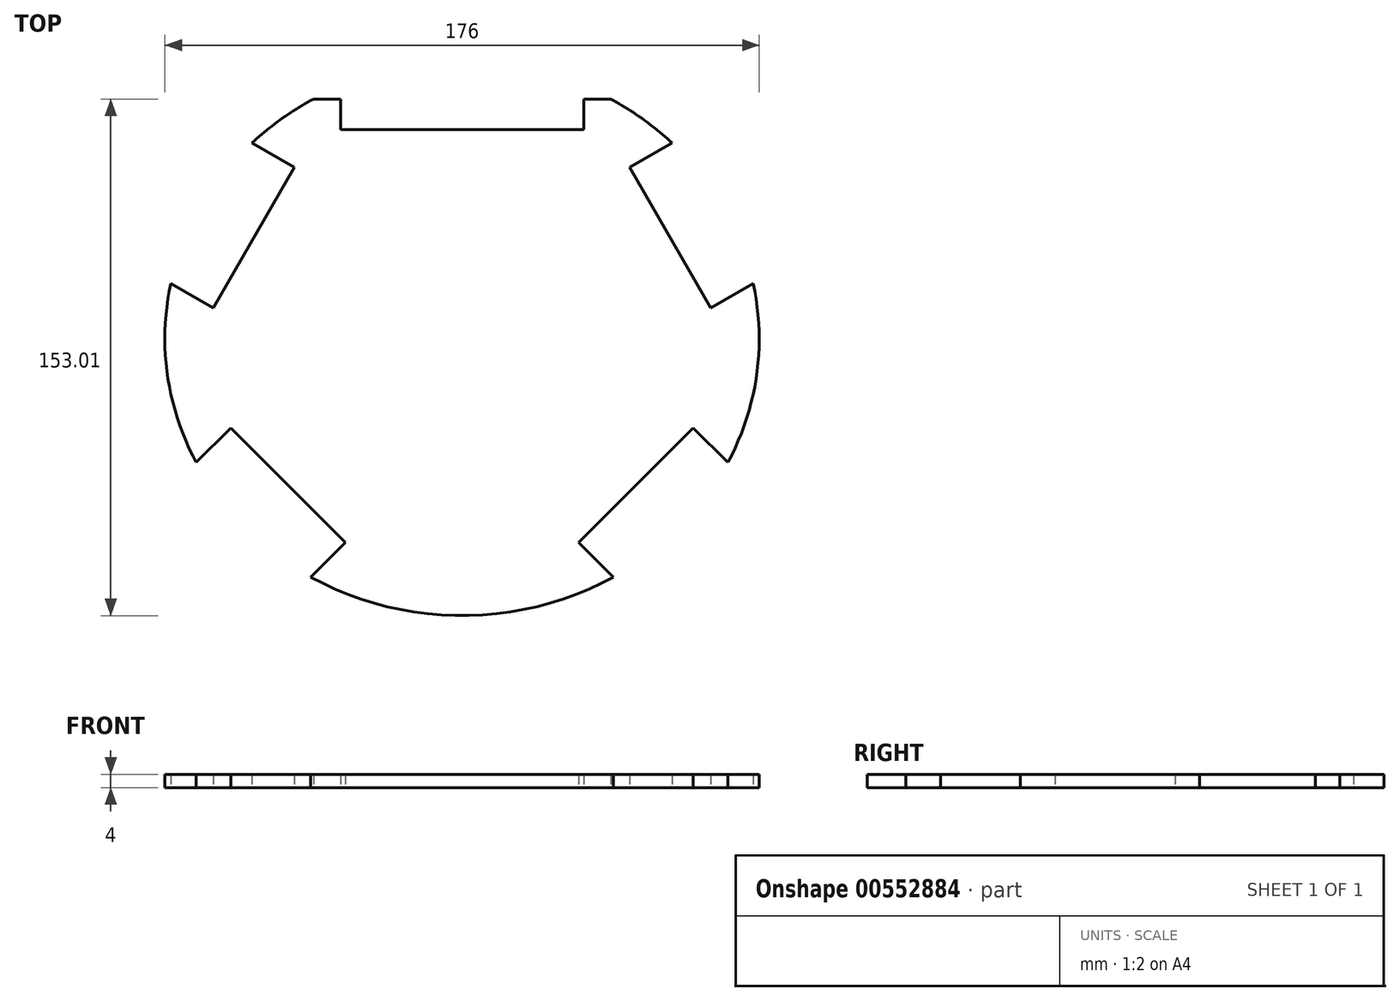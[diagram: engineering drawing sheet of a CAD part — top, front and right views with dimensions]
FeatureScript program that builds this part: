
annotation { "Feature Type Name" : "Feature", "Feature Type Description" : "" }
export const myFeature = defineFeature(function(context is Context, id is Id, definition is map)
    precondition{}
    {
        {
            var Q0;
            Q0=qCreatedBy(makeId("Top.planeOp"),FACE);
            var sketch = newSketch(context, id + "F0", { "sketchPlane" : qUnion([Q0])});
            skEllipticalArc(sketch, "E0", {});
            skLineSegment(sketch, "E1", {"start": v(-44, 71.01) * mm, "end": v(-36, 71.01) * mm});
            skLineSegment(sketch, "E2", {"start": v(-75.53, 0) * mm, "end": v(76.85, 0) * mm, "construction": true});
            skPoint(sketch, "E3.middle", {"position": v(0, 71.01) * mm});
            skLineSegment(sketch, "E4.bottom", {"start": v(36, 62.01) * mm, "end": v(-36, 62.01) * mm});
            skLineSegment(sketch, "E4.left", {"start": v(36, 62.01) * mm, "end": v(36, 71.01) * mm});
            skLineSegment(sketch, "E4.right", {"start": v(-36, 62.01) * mm, "end": v(-36, 71.01) * mm});
            skEllipticalArc(sketch, "E5.trimOffspring", {});
            skEllipticalArc(sketch, "E6.trimOffspring", {});
            skEllipticalArc(sketch, "E7.trimOffspring", {});
            skEllipticalArc(sketch, "E8.trimOffspring", {});
            skLineSegment(sketch, "E9", {"start": v(-86.22, 16.42) * mm, "end": v(-73.66, 9.17) * mm});
            skLineSegment(sketch, "E10", {"start": v(-73.66, 9.17) * mm, "end": v(-49.66, 50.74) * mm});
            skLineSegment(sketch, "E11", {"start": v(-49.66, 50.74) * mm, "end": v(-62.22, 58) * mm});
            skLineSegment(sketch, "E12", {"start": v(-78.72, -36.65) * mm, "end": v(-68.47, -26.4) * mm});
            skLineSegment(sketch, "E13", {"start": v(-68.47, -26.4) * mm, "end": v(-34.53, -60.34) * mm});
            skLineSegment(sketch, "E14", {"start": v(-34.53, -60.34) * mm, "end": v(-44.78, -70.59) * mm});
            skLineSegment(sketch, "E15", {"start": v(44.78, -70.59) * mm, "end": v(34.53, -60.34) * mm});
            skLineSegment(sketch, "E16", {"start": v(34.53, -60.34) * mm, "end": v(68.47, -26.4) * mm});
            skLineSegment(sketch, "E17", {"start": v(68.47, -26.4) * mm, "end": v(78.72, -36.65) * mm});
            skLineSegment(sketch, "E18", {"start": v(62.22, 58) * mm, "end": v(49.66, 50.74) * mm});
            skLineSegment(sketch, "E19", {"start": v(49.66, 50.74) * mm, "end": v(73.66, 9.17) * mm});
            skLineSegment(sketch, "E20", {"start": v(73.66, 9.17) * mm, "end": v(86.22, 16.42) * mm});
            skPoint(sketch, "E21.orphan", {"position": v(-36, 80.01) * mm});
            skPoint(sketch, "E22.orphan", {"position": v(36, 80.01) * mm});
            skLineSegment(sketch, "E23.trimOffspring", {"start": v(36, 71.01) * mm, "end": v(44, 71.01) * mm});
            const initialGuessF0  = {"E0": [0, 0, 0, 1, 0.082, 0.088, 0.5235987755983009, 0.7852704349621078], "E5.trimOffspring": [0, 0, 0, 1, 0.082, 0.088, 1.3691777393870463, 2.034118417076403], "E6.trimOffspring": [0, 0, 0, 1, 0.082, 0.088, 5.497914872217478, 5.759586531581288], "E7.trimOffspring": [0, 0, 0, 1, 0.082, 0.088, 2.6077116161211045, 3.675473691058483], "E8.trimOffspring": [0, 0, 0, 1, 0.082, 0.088, 4.249066890103183, 4.91400756779254]};
            skSetInitialGuess(sketch, initialGuessF0);
            skSolve(sketch);
        }
        {
            var Q0;
            Q0=makeQuery(id+"F0.imprint","IMPRINT",FACE,{"disambiguationData":[TD([[makeQuery(id+"F0.imprint","IMPRINT",EDGE,{"derivedFrom":sQuery(id+"F0.wireOp",EDGE,"E0")}),1.0]])]});
            extrude(context, id + "F1", {"entities" : qUnion([Q0]), "depth" : 4 * mm, "offsetDistance" : 25 * mm});
        }
    });
